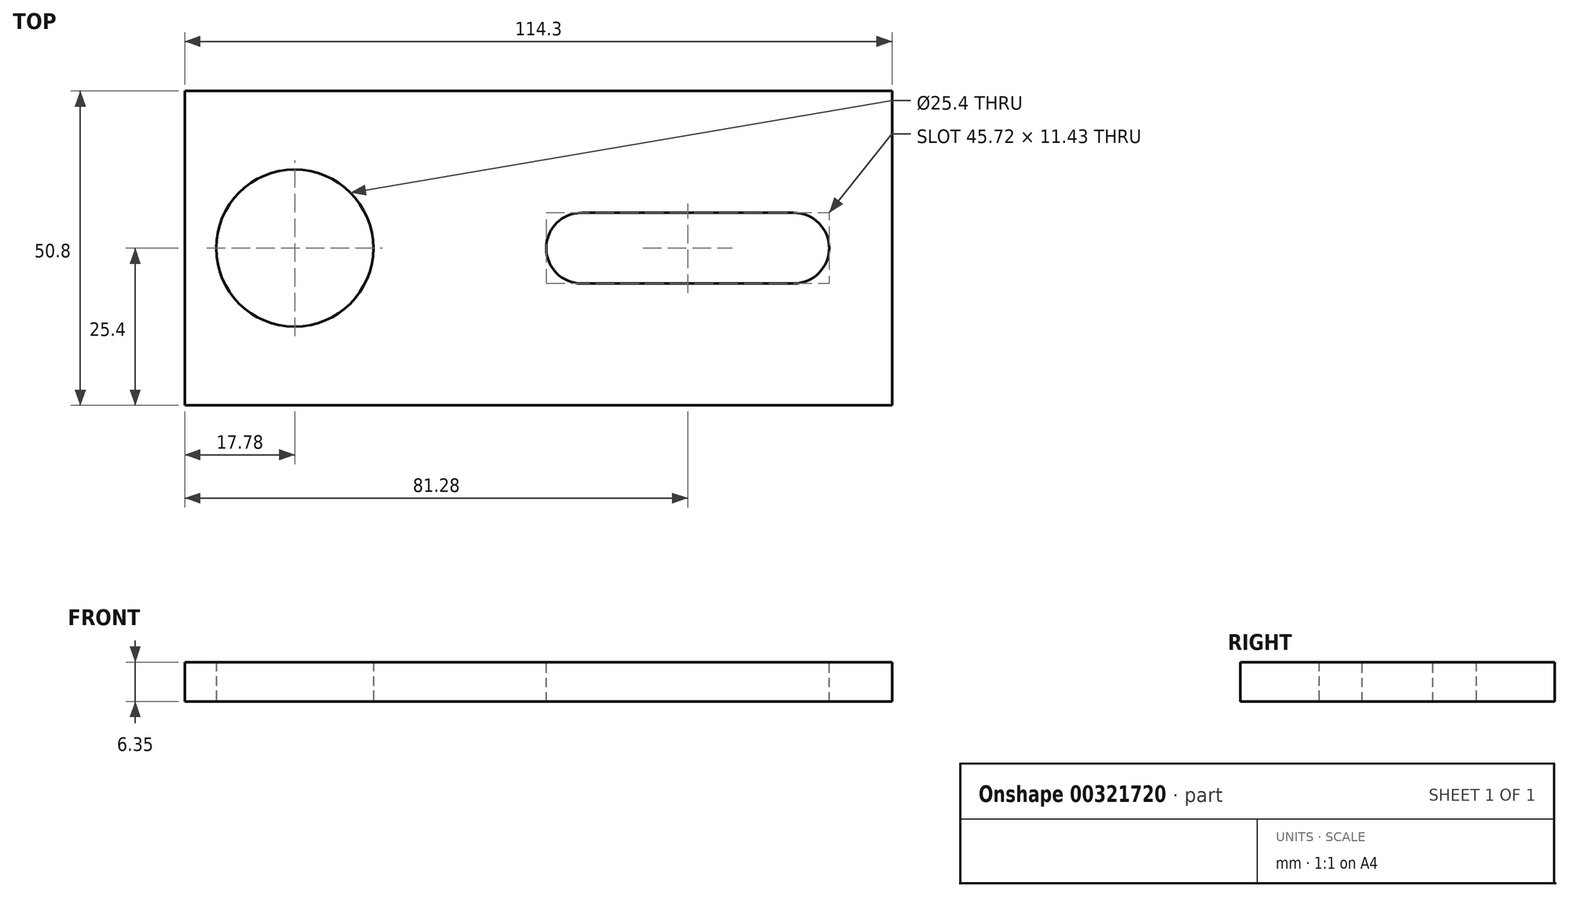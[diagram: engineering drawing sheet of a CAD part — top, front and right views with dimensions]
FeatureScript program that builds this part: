
annotation { "Feature Type Name" : "Feature", "Feature Type Description" : "" }
export const myFeature = defineFeature(function(context is Context, id is Id, definition is map)
    precondition{}
    {
        {
            var Q0;
            Q0=qCreatedBy(makeId("Top.planeOp"),FACE);
            var sketch = newSketch(context, id + "F0", { "sketchPlane" : qUnion([Q0])});
            skLineSegment(sketch, "E0.bottom", {"start": v(0, 0) * mm, "end": v(-114.3, 0) * mm});
            skLineSegment(sketch, "E0.top", {"start": v(0, 50.8) * mm, "end": v(-114.3, 50.8) * mm});
            skLineSegment(sketch, "E0.left", {"start": v(0, 0) * mm, "end": v(0, 50.8) * mm});
            skLineSegment(sketch, "E0.right", {"start": v(-114.3, 0) * mm, "end": v(-114.3, 50.8) * mm});
            skCircle(sketch, "E1", {"center": v(-96.52, 25.4) * mm, "radius": 12.7 * mm});
            skSolve(sketch);
        }
        {
            var Q0;
            Q0=makeQuery(id+"F0.imprint","IMPRINT",FACE,{"disambiguationData":[TD([[makeQuery(id+"F0.imprint","IMPRINT",EDGE,{"derivedFrom":sQuery(id+"F0.wireOp",EDGE,"E0.bottom")}),-1.0]])]});
            extrude(context, id + "F1", {"entities" : qUnion([Q0]), "depth" : 6.35 * mm});
        }
        {
            var Q0;
            Q0=makeQuery(id+"F1.opExtrude","CAP_FACE",FACE,{"disambiguationData":[OSD([sQuery(id+"F0.wireOp",EDGE,"E0.bottom"),sQuery(id+"F0.wireOp",EDGE,"E0.top"),sQuery(id+"F0.wireOp",EDGE,"E0.left"),sQuery(id+"F0.wireOp",EDGE,"E0.right"),sQuery(id+"F0.wireOp",EDGE,"E1")])],"isStart":false});
            var sketch = newSketch(context, id + "F2", { "sketchPlane" : qUnion([Q0])});
            skLineSegment(sketch, "E2.bottom", {"start": v(-15.88, 31.12) * mm, "end": v(-50.17, 31.12) * mm});
            skLineSegment(sketch, "E2.top", {"start": v(-15.88, 19.69) * mm, "end": v(-50.17, 19.69) * mm});
            skLineSegment(sketch, "E2.left", {"start": v(-15.88, 31.12) * mm, "end": v(-15.88, 19.69) * mm});
            skLineSegment(sketch, "E2.right", {"start": v(-50.17, 31.12) * mm, "end": v(-50.17, 19.69) * mm});
            skPoint(sketch, "E2.middle", {"position": v(-33.02, 25.4) * mm});
            skArc(sketch, "E3", {"start": v(-15.88, 31.12) * mm, "mid": v(-10.16, 25.4) * mm, "end": v(-15.88, 19.69) * mm});
            skArc(sketch, "E4", {"start": v(-50.17, 31.12) * mm, "mid": v(-55.88, 25.4) * mm, "end": v(-50.17, 19.69) * mm});
            skSolve(sketch);
        }
        {
            var Q0;
            Q0=makeQuery(id+"F2.imprint","IMPRINT",FACE,{"disambiguationData":[TD([[makeQuery(id+"F2.imprint","IMPRINT",EDGE,{"derivedFrom":sQuery(id+"F2.wireOp",EDGE,"E2.bottom")}),1.0]])]});
            var Q1;
            Q1=makeQuery(id+"F2.imprint","IMPRINT",FACE,{"disambiguationData":[TD([[makeQuery(id+"F2.imprint","IMPRINT",EDGE,{"derivedFrom":sQuery(id+"F2.wireOp",EDGE,"E2.right")}),-1.0]])]});
            var Q2;
            Q2=makeQuery(id+"F2.imprint","IMPRINT",FACE,{"disambiguationData":[TD([[makeQuery(id+"F2.imprint","IMPRINT",EDGE,{"derivedFrom":sQuery(id+"F2.wireOp",EDGE,"E2.left")}),1.0]])]});
            extrude(context, id + "F3", {"entities" : qUnion([Q0, Q1, Q2]), "operationType" : NewBodyOperationType.REMOVE, "oppositeDirection" : true, "depth" : 25.4 * mm});
        }
    });
